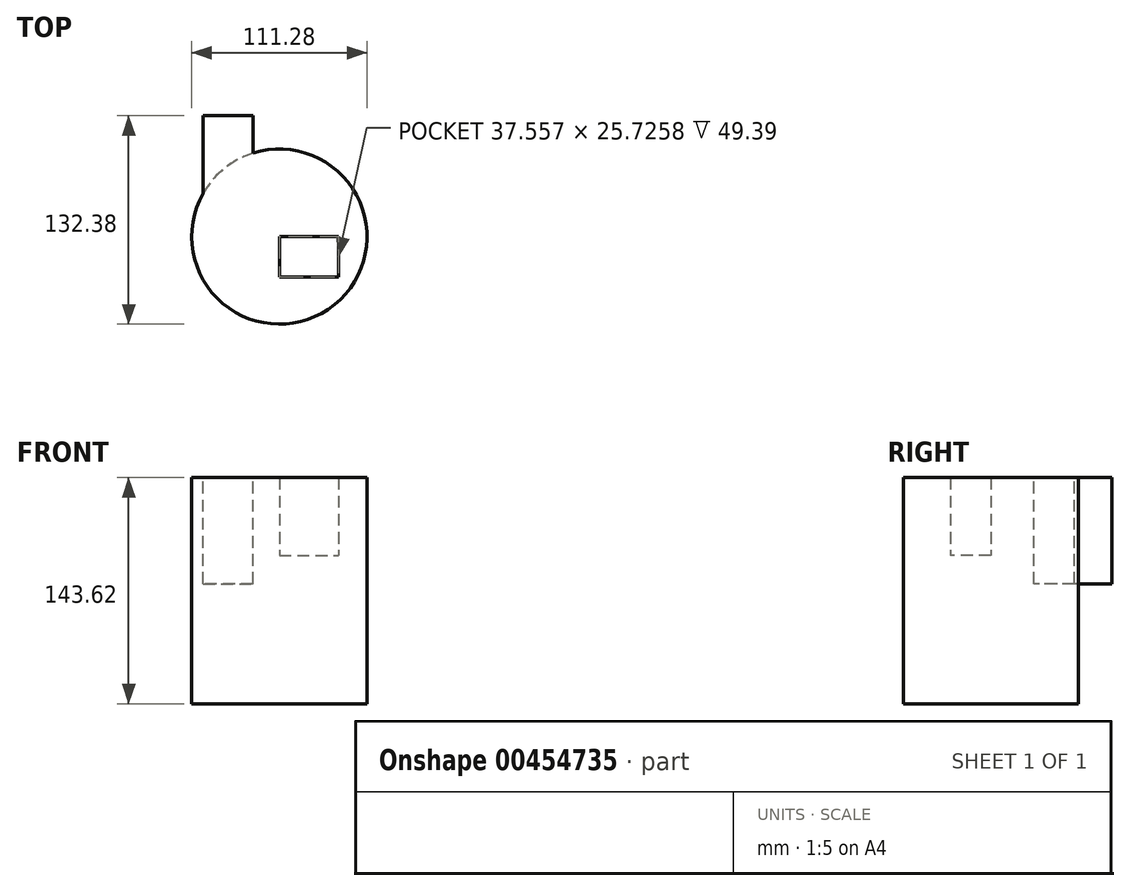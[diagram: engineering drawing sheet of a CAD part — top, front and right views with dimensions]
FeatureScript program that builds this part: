
annotation { "Feature Type Name" : "Feature", "Feature Type Description" : "" }
export const myFeature = defineFeature(function(context is Context, id is Id, definition is map)
    precondition{}
    {
        {
            var Q0;
            Q0=qCreatedBy(makeId("Top.planeOp"),FACE);
            var sketch = newSketch(context, id + "F0", { "sketchPlane" : qUnion([Q0])});
            skCircle(sketch, "E0", {"center": v(0, 0) * mm, "radius": 55.64 * mm});
            skSolve(sketch);
        }
        {
            var Q0;
            Q0=makeQuery(id+"F0.imprint","IMPRINT",FACE,{"disambiguationData":[TD([[makeQuery(id+"F0.imprint","IMPRINT",EDGE,{"derivedFrom":sQuery(id+"F0.wireOp",EDGE,"E0")}),1.0]])]});
            extrude(context, id + "F1", {"entities" : qUnion([Q0]), "depth" : 94.23 * mm});
        }
        {
            var Q0;
            Q0=makeQuery(id+"F1.opExtrude","CAP_FACE",FACE,{"disambiguationData":[OSD([sQuery(id+"F0.wireOp",EDGE,"E0")])],"isStart":false});
            var sketch = newSketch(context, id + "F2", { "sketchPlane" : qUnion([Q0])});
            skLineSegment(sketch, "E1.bottom", {"start": v(92.1, 98.14) * mm, "end": v(-92.1, 98.14) * mm});
            skLineSegment(sketch, "E1.top", {"start": v(92.1, -98.14) * mm, "end": v(-92.1, -98.14) * mm});
            skLineSegment(sketch, "E1.left", {"start": v(92.1, 98.14) * mm, "end": v(92.1, -98.14) * mm});
            skLineSegment(sketch, "E1.right", {"start": v(-92.1, 98.14) * mm, "end": v(-92.1, -98.14) * mm});
            skPoint(sketch, "E1.middle", {"position": v(0, 0) * mm});
            skSolve(sketch);
        }
        {
            var Q0;
            Q0=makeQuery(id+"F2.imprint","IMPRINT",FACE,{"disambiguationData":[TD([[makeQuery(id+"F2.imprint","IMPRINT",EDGE,{"derivedFrom":makeQuery(id+"F1.opExtrude","CAP_EDGE",EDGE,{"disambiguationData":[OSD([sQuery(id+"F0.wireOp",EDGE,"E0")])],"isStart":false})}),1.0]])]});
            var sketch = newSketch(context, id + "F3", { "sketchPlane" : qUnion([Q0])});
            skLineSegment(sketch, "E2", {"start": v(0, -25.73) * mm, "end": v(37.56, -25.73) * mm});
            skLineSegment(sketch, "E3", {"start": v(37.56, -25.73) * mm, "end": v(37.56, 0) * mm});
            skLineSegment(sketch, "E4", {"start": v(37.56, 0) * mm, "end": v(0, 0) * mm});
            skLineSegment(sketch, "E5", {"start": v(0, 0) * mm, "end": v(0, -25.73) * mm});
            skSolve(sketch);
        }
        {
            var Q0;
            Q0=makeQuery(id+"F3.imprint","IMPRINT",FACE,{"disambiguationData":[TD([[makeQuery(id+"F3.imprint","IMPRINT",EDGE,{"derivedFrom":sQuery(id+"F3.wireOp",EDGE,"E2")}),-1.0]])]});
            extrude(context, id + "F4", {"entities" : qUnion([Q0]), "operationType" : NewBodyOperationType.ADD, "depth" : 49.4 * mm, "offsetDistance" : 25.4 * mm});
        }
        {
            var Q0;
            Q0=makeQuery(id+"F4.opExtrude","CAP_FACE",FACE,{"disambiguationData":[OSD([sQuery(id+"F0.wireOp",EDGE,"E0"),sQuery(id+"F3.wireOp",EDGE,"E2"),sQuery(id+"F3.wireOp",EDGE,"E3"),sQuery(id+"F3.wireOp",EDGE,"E4"),sQuery(id+"F3.wireOp",EDGE,"E5")])],"isStart":false});
            var sketch = newSketch(context, id + "F5", { "sketchPlane" : qUnion([Q0])});
            skLineSegment(sketch, "E6.bottom", {"start": v(-39.78, 0) * mm, "end": v(-25.7, 0) * mm});
            skLineSegment(sketch, "E6.top", {"start": v(-39.78, 0) * mm, "end": v(-25.7, 0) * mm});
            skLineSegment(sketch, "E6.left", {"start": v(-39.78, 0) * mm, "end": v(-39.78, 0) * mm});
            skLineSegment(sketch, "E6.right", {"start": v(-25.7, 0) * mm, "end": v(-25.7, 0) * mm});
            skLineSegment(sketch, "E7.bottom", {"start": v(-48.4, 76.74) * mm, "end": v(-16.78, 76.74) * mm});
            skLineSegment(sketch, "E7.top", {"start": v(-48.4, 0) * mm, "end": v(-16.78, 0) * mm});
            skLineSegment(sketch, "E7.left", {"start": v(-48.4, 76.74) * mm, "end": v(-48.4, 0) * mm});
            skLineSegment(sketch, "E7.right", {"start": v(-16.78, 76.74) * mm, "end": v(-16.78, 0) * mm});
            skSolve(sketch);
        }
        {
            var Q0;
            {var subQ0=sQuery(id+"F5.wireOp",EDGE,"E7.bottom");Q0=makeQuery(id+"F5.imprint","IMPRINT",FACE,{"disambiguationData":[TD([[makeQuery(id+"F5.imprint","IMPRINT",EDGE,{"derivedFrom":subQ0}),-1.0]])]});}
            var Q1;
            {var subQ1=sQuery(id+"F5.wireOp",EDGE,"E7.top");var subQ8=makeQuery(id+"F5.imprint","IMPRINT",VERTEX,{"disambiguationData":[OD(0.0)],"derivedFrom":subQ1});Q1=makeQuery(id+"F5.imprint","IMPRINT",FACE,{"disambiguationData":[TD([[makeQuery(id+"F5.imprint","IMPRINT",EDGE,{"disambiguationData":[TD([[subQ8,-1.0]])],"derivedFrom":subQ1}),1.0]])]});}
            extrude(context, id + "F6", {"entities" : qUnion([Q0, Q1]), "operationType" : NewBodyOperationType.ADD, "oppositeDirection" : true, "depth" : 67.54 * mm, "offsetDistance" : 25.4 * mm});
        }
    });
